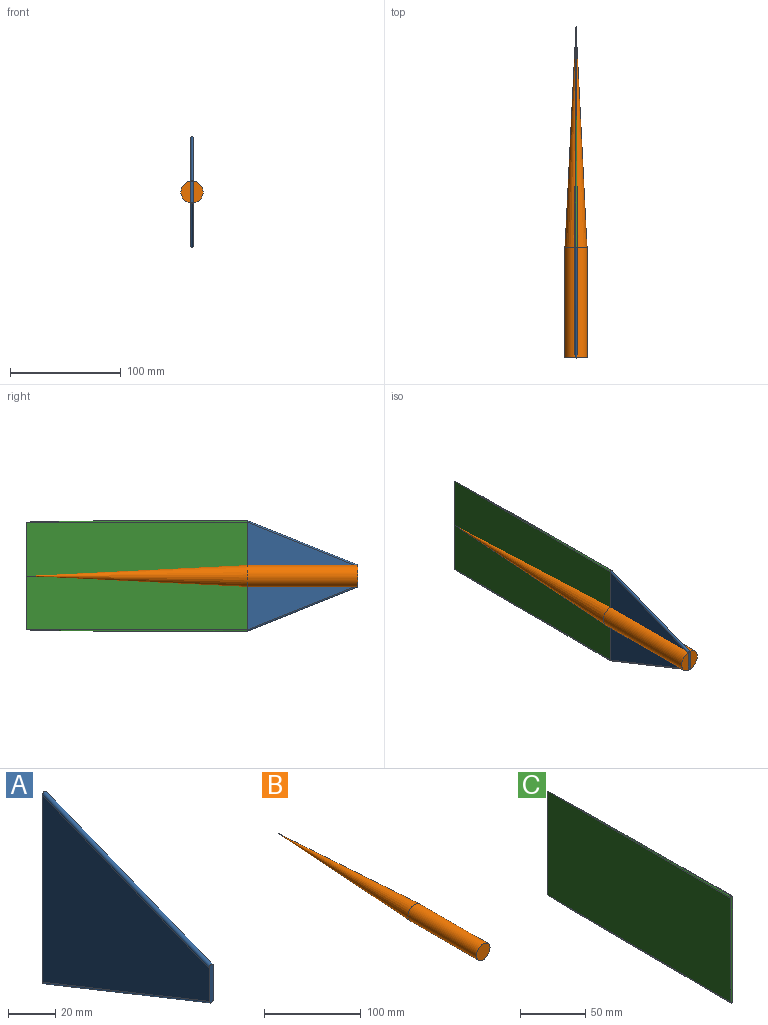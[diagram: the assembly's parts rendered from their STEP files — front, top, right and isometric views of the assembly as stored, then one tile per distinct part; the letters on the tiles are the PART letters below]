
ASSEMBLY  parts=3 mates=2
PART A: 6 faces, bbox 2.5x100.9x100 mm
  f0: plane 20x2.5mm, normal (0,-1,0), area 48.6mm2, adj f2,f3,f4,f5
  f1: plane 100x2.5mm, normal (0,1,0), area 248.6mm2, adj f2,f3,f4,f5
  f2: plane 100x97.31mm, normal (1,0,0), area 5730.7mm2, adj f0,f1,f4,f5
  f3: plane 100x97.31mm, normal (-1,0,0), area 5730.7mm2, adj f0,f1,f4,f5
  f4: cylinder r=1.25mm len=100.93mm, axis (0,0.93,0.37), area 422.9mm2, adj f0,f1,f2,f3
  f5: cylinder r=1.25mm len=100.93mm, axis (0,-0.93,0.37), area 422.9mm2, adj f0,f1,f2,f3
PART B: 3 faces, bbox 20x300x20 mm
  f0: cone r=10mm half-angle=2.9deg, axis (0,-1,0), area 6291mm2, adj f1
  f1: cylinder r=10mm len=100mm, axis (0,-1,0), area 6283.2mm2, adj f0,f2
  f2: plane 20x20mm, normal (0,-1,0), area 314.2mm2, adj f1
PART C: 7 faces, bbox 2.8x240x100 mm
  f0: plane 200x97.5mm, normal (1,0.01,0), area 19500.4mm2, adj f1,f2,f4,f6
  f1: plane 200x97.5mm, normal (-1,0.01,0), area 19500.4mm2, adj f0,f2,f3,f5
  f2: plane 100x2.5mm, normal (0,-1,0), area 249mm2, adj f0,f1,f3,f4,f5,f6
  f3: bspline ~240.01x2.75mm, area 267.2mm2, adj f1,f2,f4
  f4: bspline ~240.01x2.75mm, area 267.2mm2, adj f0,f2,f3
  f5: bspline ~240.01x2.75mm, area 267.2mm2, adj f1,f2,f6
  f6: bspline ~240.01x2.75mm, area 267.2mm2, adj f0,f2,f5
PLACE A at identity
PLACE B at identity fixed
PLACE C at identity
MATE fastened C.f2 <-> B.f0  axis (0,-1,0) through (0,0,0)mm
MATE fastened A.f0 <-> B.f0  axis (0,-1,0) through (0,-100,0)mm
